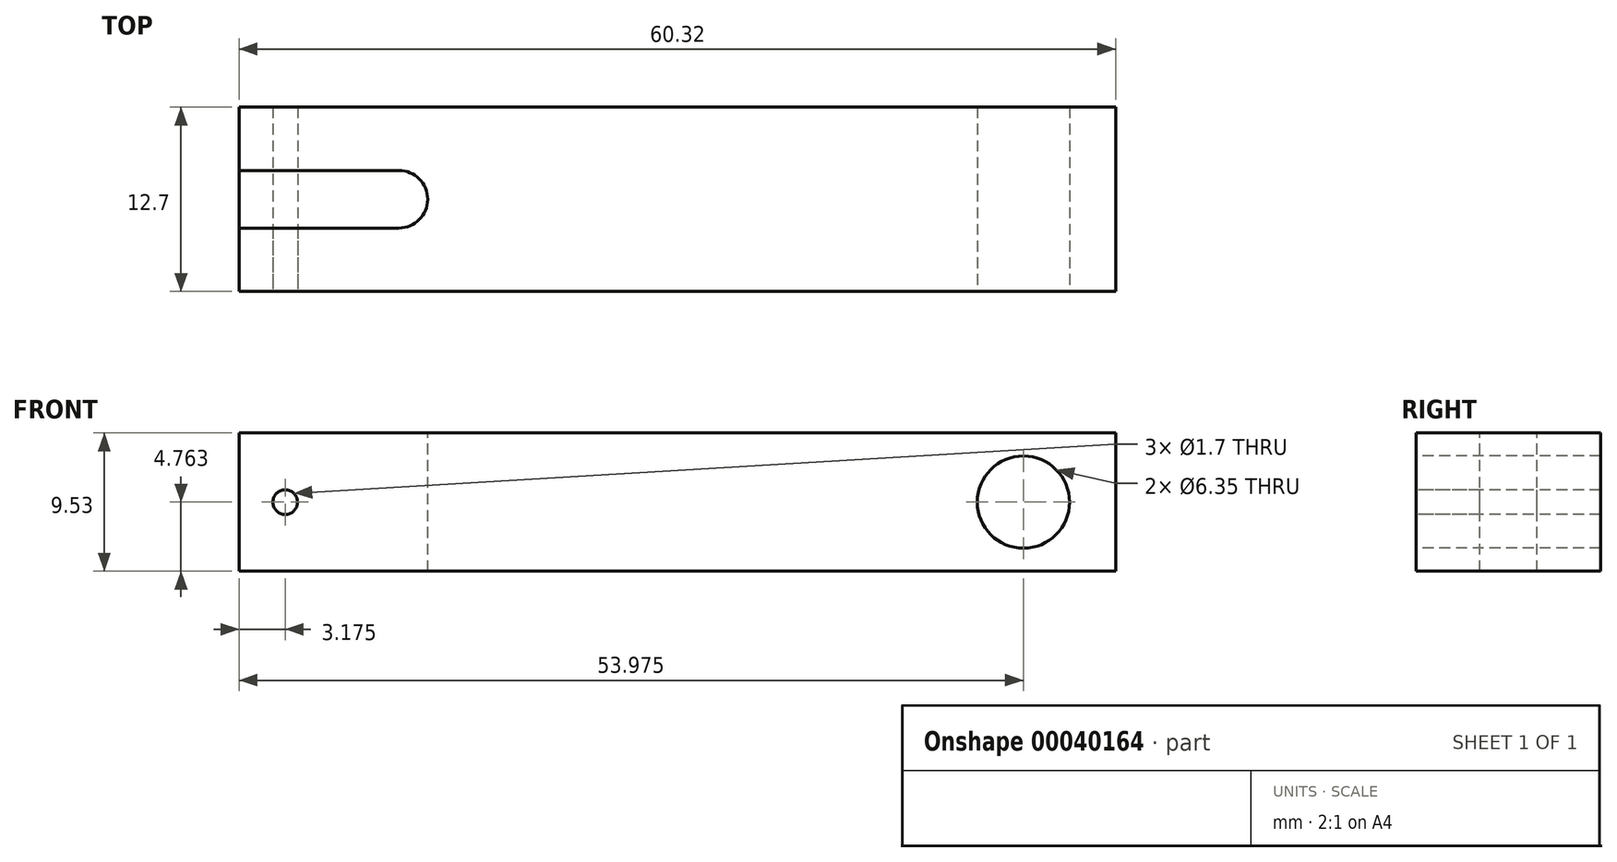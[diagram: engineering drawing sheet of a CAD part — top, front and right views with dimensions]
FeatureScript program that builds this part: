
annotation { "Feature Type Name" : "Feature", "Feature Type Description" : "" }
export const myFeature = defineFeature(function(context is Context, id is Id, definition is map)
    precondition{}
    {
        {
            var Q0;
            Q0=qCreatedBy(makeId("Front.planeOp"),FACE);
            var sketch = newSketch(context, id + "F0", { "sketchPlane" : qUnion([Q0])});
            skLineSegment(sketch, "E0.bottom", {"start": v(0, 0) * mm, "end": v(60.33, 0) * mm});
            skLineSegment(sketch, "E0.top", {"start": v(0, 9.53) * mm, "end": v(60.33, 9.53) * mm});
            skLineSegment(sketch, "E0.left", {"start": v(0, 0) * mm, "end": v(0, 9.53) * mm});
            skLineSegment(sketch, "E0.right", {"start": v(60.33, 0) * mm, "end": v(60.33, 9.53) * mm});
            skPoint(sketch, "E1", {"position": v(3.18, 4.76) * mm});
            skPoint(sketch, "E2", {"position": v(53.98, 4.76) * mm});
            skLineSegment(sketch, "E3", {"start": v(0, 4.76) * mm, "end": v(60.33, 4.76) * mm, "construction": true});
            skCircle(sketch, "E4", {"center": v(3.18, 4.76) * mm, "radius": 0.85 * mm});
            skCircle(sketch, "E5", {"center": v(53.98, 4.76) * mm, "radius": 3.18 * mm});
            skSolve(sketch);
        }
        {
            var Q0;
            Q0=makeQuery(id+"F0.imprint","IMPRINT",FACE,{"disambiguationData":[TD([[makeQuery(id+"F0.imprint","IMPRINT",EDGE,{"derivedFrom":sQuery(id+"F0.wireOp",EDGE,"E0.bottom")}),1.0]])]});
            extrude(context, id + "F1", {"entities" : qUnion([Q0]), "oppositeDirection" : true, "depth" : 12.7 * mm});
        }
        {
            var Q0;
            Q0=makeQuery(id+"F1.opExtrude","SWEPT_FACE",FACE,{"disambiguationData":[OSD([sQuery(id+"F0.wireOp",EDGE,"E0.top")])]});
            var sketch = newSketch(context, id + "F2", { "sketchPlane" : qUnion([Q0])});
            skLineSegment(sketch, "E6", {"start": v(0, 6.35) * mm, "end": v(60.33, 6.35) * mm, "construction": true});
            skLineSegment(sketch, "E7", {"start": v(0, 8.33) * mm, "end": v(11, 8.33) * mm});
            skArc(sketch, "E8", {"start": v(12.98, 6.35) * mm, "mid": v(12.4, 7.75) * mm, "end": v(11, 8.33) * mm});
            skLineSegment(sketch, "E9", {"start": v(11, 8.33) * mm, "end": v(11, 6.35) * mm, "construction": true});
            skArc(sketch, "E10.MirrorCS", {"start": v(12.98, 6.35) * mm, "mid": v(12.4, 4.95) * mm, "end": v(11, 4.37) * mm});
            skLineSegment(sketch, "E11.MirrorCS", {"start": v(0, 4.37) * mm, "end": v(11, 4.37) * mm});
            skLineSegment(sketch, "E12", {"start": v(0, 8.33) * mm, "end": v(0, 4.37) * mm});
            skSolve(sketch);
        }
        {
            var Q0;
            Q0=makeQuery(id+"F2.imprint","IMPRINT",FACE,{"disambiguationData":[TD([[makeQuery(id+"F2.imprint","IMPRINT",EDGE,{"derivedFrom":sQuery(id+"F2.wireOp",EDGE,"E7")}),-1.0]])]});
            extrude(context, id + "F3", {"entities" : qUnion([Q0]), "operationType" : NewBodyOperationType.REMOVE, "endBound" : BoundingType.THROUGH_ALL, "oppositeDirection" : true, "depth" : 25.4 * mm});
        }
        {
            var Q0;
            Q0=makeQuery(id+"F0.imprint","IMPRINT",FACE,{"disambiguationData":[TD([[makeQuery(id+"F0.imprint","IMPRINT",EDGE,{"derivedFrom":sQuery(id+"F0.wireOp",EDGE,"E0.bottom")}),1.0]])]});
            extrude(context, id + "F4", {"entities" : qUnion([Q0]), "oppositeDirection" : true, "depth" : 12.7 * mm});
        }
    });
